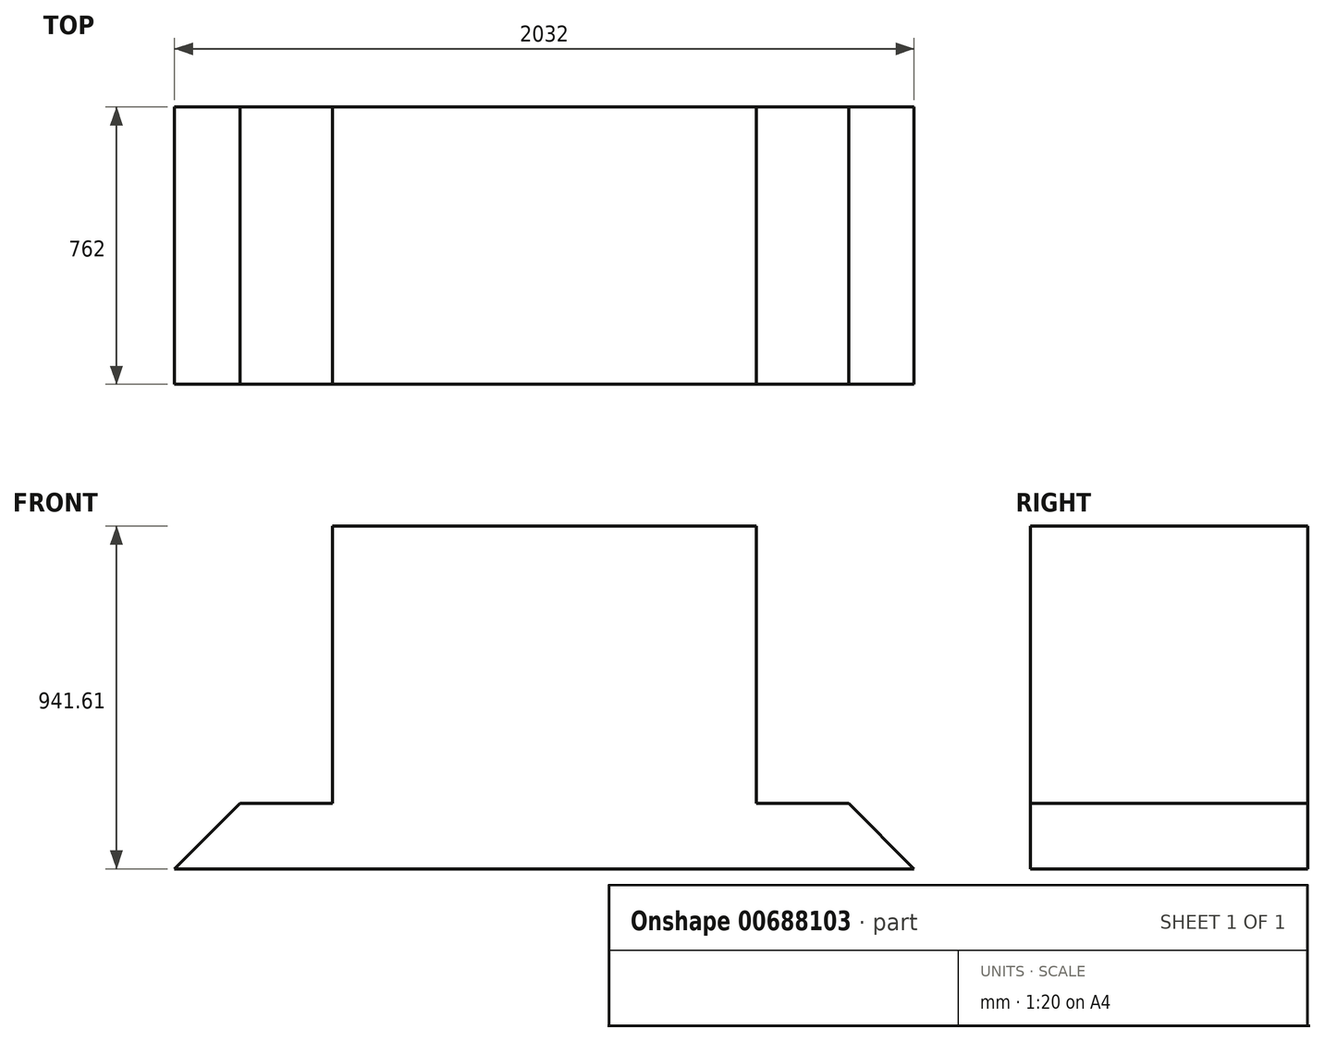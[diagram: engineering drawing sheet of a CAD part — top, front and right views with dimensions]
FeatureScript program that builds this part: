
annotation { "Feature Type Name" : "Feature", "Feature Type Description" : "" }
export const myFeature = defineFeature(function(context is Context, id is Id, definition is map)
    precondition{}
    {
        {
            var Q0;
            Q0=qCreatedBy(makeId("Front.planeOp"),FACE);
            var sketch = newSketch(context, id + "F0", { "sketchPlane" : qUnion([Q0])});
            skLineSegment(sketch, "E0", {"start": v(-1013.08, 0) * mm, "end": v(1018.92, 0) * mm});
            skLineSegment(sketch, "E1", {"start": v(1018.92, 0) * mm, "end": v(839.32, 179.6) * mm});
            skLineSegment(sketch, "E2", {"start": v(839.32, 179.6) * mm, "end": v(585.32, 179.6) * mm});
            skLineSegment(sketch, "E3", {"start": v(585.32, 179.6) * mm, "end": v(585.32, 941.6) * mm});
            skLineSegment(sketch, "E4", {"start": v(585.32, 941.6) * mm, "end": v(-579.47, 941.6) * mm});
            skLineSegment(sketch, "E5", {"start": v(-579.47, 941.6) * mm, "end": v(-579.47, 179.6) * mm});
            skLineSegment(sketch, "E6", {"start": v(-579.47, 179.6) * mm, "end": v(-833.47, 179.6) * mm});
            skLineSegment(sketch, "E7", {"start": v(-833.47, 179.6) * mm, "end": v(-1013.08, 0) * mm});
            skSolve(sketch);
        }
        {
            var Q0;
            Q0 = qSketchRegion(id + "F0", true);
            extrude(context, id + "F1", {"entities" : qUnion([Q0]), "depth" : 762 * mm, "offsetDistance" : 25.4 * mm});
        }
        {
            var Q0;
            Q0 = qSketchRegion(id + "F0", true);
            extrude(context, id + "F2", {"entities" : qUnion([Q0]), "depth" : 762 * mm, "offsetDistance" : 25.4 * mm});
        }
        {
            var Q0;
            Q0=makeQuery(id+"F1.opExtrude","SWEPT_FACE",FACE,{"disambiguationData":[OSD([sQuery(id+"F0.wireOp",EDGE,"E4")])]});
            var sketch = newSketch(context, id + "F3", { "sketchPlane" : qUnion([Q0])});
            skSolve(sketch);
        }
    });
